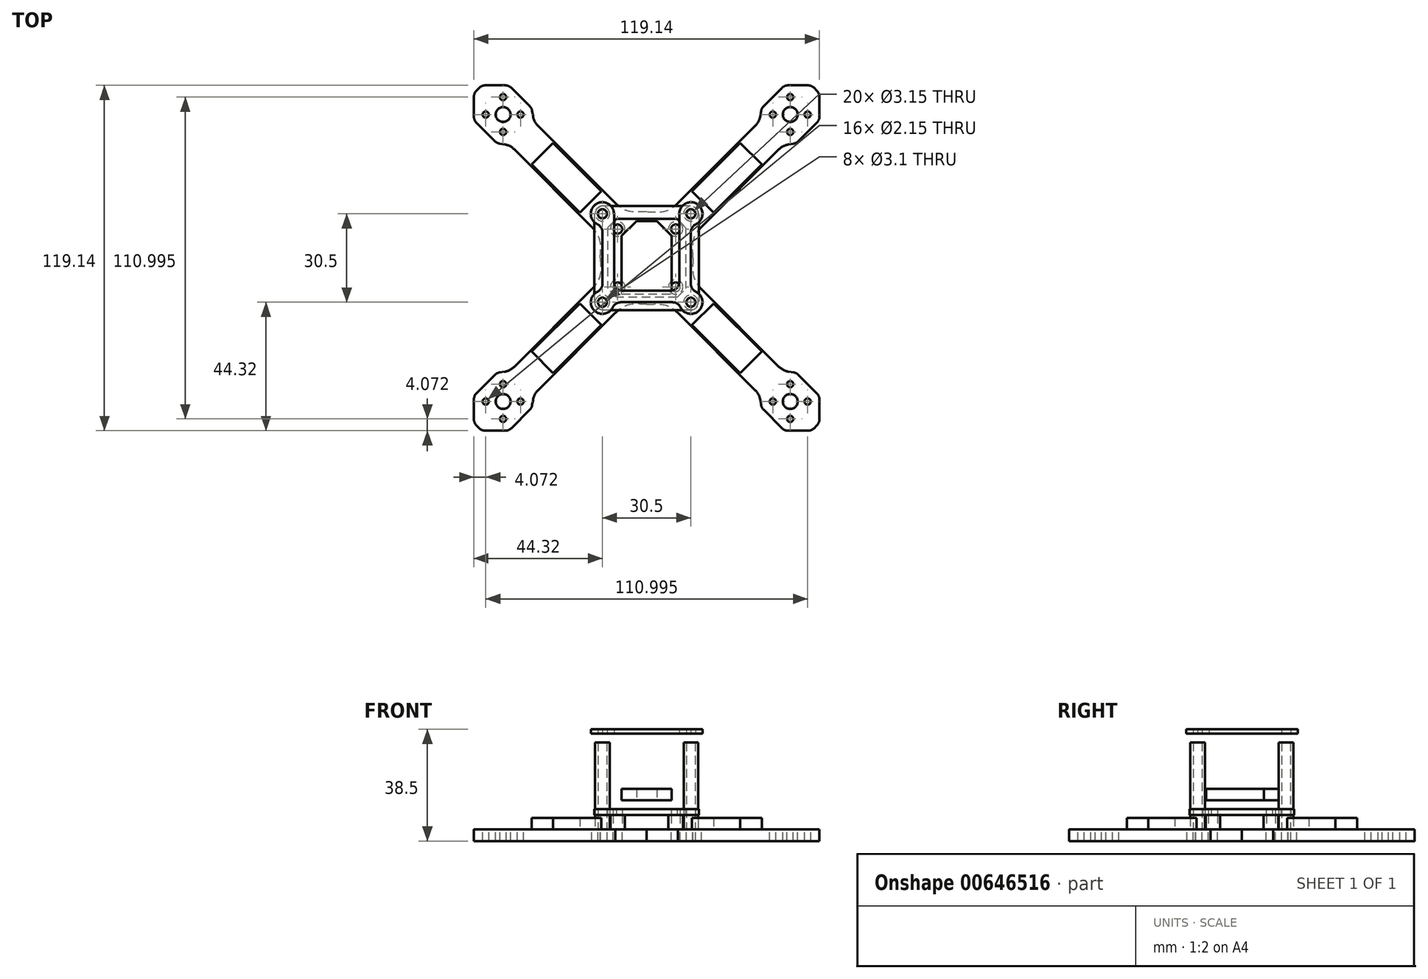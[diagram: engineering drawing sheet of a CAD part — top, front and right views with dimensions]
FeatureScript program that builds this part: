
annotation { "Feature Type Name" : "Feature", "Feature Type Description" : "" }
export const myFeature = defineFeature(function(context is Context, id is Id, definition is map)
    precondition{}
    {
        {
            var Q0;
            Q0=qCreatedBy(makeId("Top.planeOp"),FACE);
            var sketch = newSketch(context, id + "F0", { "sketchPlane" : qUnion([Q0])});
            skCircle(sketch, "E0.1", {"center": v(15.25, 15.25) * mm, "radius": 1.57 * mm});
            skLineSegment(sketch, "E1", {"start": v(49.5, 55.5) * mm, "end": v(49.5, 43.5) * mm, "construction": true});
            skLineSegment(sketch, "E2", {"start": v(45.25, 53.74) * mm, "end": v(53.74, 45.25) * mm, "construction": true});
            skCircle(sketch, "E3.MirrorC", {"center": v(49.5, 49.5) * mm, "radius": 2.58 * mm});
            skLineSegment(sketch, "E4", {"start": v(43.5, 49.5) * mm, "end": v(55.5, 49.5) * mm, "construction": true});
            skCircle(sketch, "E5", {"center": v(49.5, 49.5) * mm, "radius": 6 * mm, "construction": true});
            skCircle(sketch, "E6", {"center": v(43.5, 49.5) * mm, "radius": 1.07 * mm});
            skCircle(sketch, "E7.MirrorC", {"center": v(55.5, 49.5) * mm, "radius": 1.07 * mm});
            skCircle(sketch, "E8.MirrorC", {"center": v(49.5, 55.5) * mm, "radius": 1.07 * mm});
            skCircle(sketch, "E9.MirrorC", {"center": v(49.5, 43.5) * mm, "radius": 1.07 * mm});
            skLineSegment(sketch, "E10", {"start": v(0, 78.07) * mm, "end": v(0, -78.07) * mm, "construction": true});
            skLineSegment(sketch, "E11", {"start": v(-70, 0) * mm, "end": v(70, 0) * mm, "construction": true});
            skCircle(sketch, "E12.MirrorC", {"center": v(-15.25, 15.25) * mm, "radius": 1.57 * mm});
            skCircle(sketch, "E13.MirrorC", {"center": v(-15.25, -15.25) * mm, "radius": 1.57 * mm});
            skCircle(sketch, "E14.MirrorC", {"center": v(15.25, -15.25) * mm, "radius": 1.57 * mm});
            skLineSegment(sketch, "E15", {"start": v(49.5, 49.5) * mm, "end": v(-49.5, -49.5) * mm, "construction": true});
            skLineSegment(sketch, "E16", {"start": v(-49.5, 49.5) * mm, "end": v(49.5, -49.5) * mm, "construction": true});
            skLineSegment(sketch, "E17", {"start": v(10.78, 18.91) * mm, "end": v(18.91, 10.78) * mm, "construction": true});
            skPoint(sketch, "E18", {"position": v(14.85, 14.85) * mm});
            skPoint(sketch, "E19", {"position": v(0, 16) * mm});
            skLineSegment(sketch, "E20", {"start": v(49.5, 49.5) * mm, "end": v(67.48, 67.48) * mm, "construction": true});
            skCircle(sketch, "E21.MirrorC", {"center": v(55.5, -49.5) * mm, "radius": 1.07 * mm});
            skCircle(sketch, "E22.MirrorC", {"center": v(49.5, -43.5) * mm, "radius": 1.07 * mm});
            skLineSegment(sketch, "E23.MirrorCS", {"start": v(45.25, -53.74) * mm, "end": v(53.74, -45.25) * mm, "construction": true});
            skCircle(sketch, "E24.MirrorC", {"center": v(49.5, -55.5) * mm, "radius": 1.07 * mm});
            skLineSegment(sketch, "E25.MirrorCS", {"start": v(49.5, -55.5) * mm, "end": v(49.5, -43.5) * mm, "construction": true});
            skLineSegment(sketch, "E26.MirrorCS", {"start": v(43.5, -49.5) * mm, "end": v(55.5, -49.5) * mm, "construction": true});
            skCircle(sketch, "E27.MirrorC", {"center": v(43.5, -49.5) * mm, "radius": 1.07 * mm});
            skPoint(sketch, "E28.MirrorP", {"position": v(49.5, -49.5) * mm});
            skCircle(sketch, "E29.MirrorC", {"center": v(49.5, -49.5) * mm, "radius": 6 * mm, "construction": true});
            skCircle(sketch, "E30.MirrorC", {"center": v(49.5, -49.5) * mm, "radius": 2.58 * mm});
            skCircle(sketch, "E31.MirrorC", {"center": v(-49.5, -55.5) * mm, "radius": 1.07 * mm});
            skCircle(sketch, "E32.MirrorC", {"center": v(-43.5, -49.5) * mm, "radius": 1.07 * mm});
            skCircle(sketch, "E33.MirrorC", {"center": v(-55.5, -49.5) * mm, "radius": 1.07 * mm});
            skCircle(sketch, "E34.MirrorC", {"center": v(-49.5, -43.5) * mm, "radius": 1.07 * mm});
            skLineSegment(sketch, "E35.MirrorCS", {"start": v(-45.25, -53.74) * mm, "end": v(-53.74, -45.25) * mm, "construction": true});
            skLineSegment(sketch, "E36.MirrorCS", {"start": v(-43.5, -49.5) * mm, "end": v(-55.5, -49.5) * mm, "construction": true});
            skLineSegment(sketch, "E37.MirrorCS", {"start": v(-49.5, -55.5) * mm, "end": v(-49.5, -43.5) * mm, "construction": true});
            skPoint(sketch, "E38.MirrorP", {"position": v(-49.5, -49.5) * mm});
            skCircle(sketch, "E39.MirrorC", {"center": v(-49.5, -49.5) * mm, "radius": 6 * mm, "construction": true});
            skCircle(sketch, "E40.MirrorC", {"center": v(-49.5, -49.5) * mm, "radius": 2.58 * mm});
            skCircle(sketch, "E41.MirrorC", {"center": v(-49.5, 55.5) * mm, "radius": 1.07 * mm});
            skCircle(sketch, "E42.MirrorC", {"center": v(-43.5, 49.5) * mm, "radius": 1.07 * mm});
            skCircle(sketch, "E43.MirrorC", {"center": v(-49.5, 43.5) * mm, "radius": 1.07 * mm});
            skCircle(sketch, "E44.MirrorC", {"center": v(-55.5, 49.5) * mm, "radius": 1.07 * mm});
            skLineSegment(sketch, "E45.MirrorCS", {"start": v(-45.25, 53.74) * mm, "end": v(-53.74, 45.25) * mm, "construction": true});
            skLineSegment(sketch, "E46.MirrorCS", {"start": v(-43.5, 49.5) * mm, "end": v(-55.5, 49.5) * mm, "construction": true});
            skLineSegment(sketch, "E47.MirrorCS", {"start": v(-49.5, 55.5) * mm, "end": v(-49.5, 43.5) * mm, "construction": true});
            skPoint(sketch, "E48.MirrorP", {"position": v(-49.5, 49.5) * mm});
            skCircle(sketch, "E49.MirrorC", {"center": v(-49.5, 49.5) * mm, "radius": 6 * mm, "construction": true});
            skCircle(sketch, "E50.MirrorC", {"center": v(-49.5, 49.5) * mm, "radius": 2.58 * mm});
            skCircle(sketch, "E51.MirrorC", {"center": v(10, 10) * mm, "radius": 1.57 * mm});
            skCircle(sketch, "E52.MirrorC", {"center": v(10, -10) * mm, "radius": 1.57 * mm});
            skCircle(sketch, "E53.MirrorC", {"center": v(-10, -10) * mm, "radius": 1.57 * mm});
            skCircle(sketch, "E54.MirrorC", {"center": v(-10, 10) * mm, "radius": 1.57 * mm});
            skLineSegment(sketch, "E55", {"start": v(16, 8) * mm, "end": v(16, -8) * mm, "construction": true});
            skPoint(sketch, "E56", {"position": v(16, 0) * mm});
            skPoint(sketch, "E57", {"position": v(0, 0) * mm});
            skPoint(sketch, "E58", {"position": v(-27.66, 27.66) * mm});
            skPoint(sketch, "E59", {"position": v(6.88, 16.35) * mm});
            skFitSpline(sketch, "E60", {"points": [v(0, 16) * mm, v(6.88, 16.35) * mm, v(10.78, 18.91) * mm], "startDerivative": vector(12.86, -0.37) * mm, "endDerivative": vector(5.42, 4.33) * mm});
            skLineSegment(sketch, "E61", {"start": v(10.78, 18.91) * mm, "end": v(37.5, 45.63) * mm});
            skLineSegment(sketch, "E62", {"start": v(39.18, 48.92) * mm, "end": v(39.46, 50.68) * mm});
            skLineSegment(sketch, "E63", {"start": v(40.3, 52.33) * mm, "end": v(46.67, 58.69) * mm});
            skLineSegment(sketch, "E64", {"start": v(48.8, 59.57) * mm, "end": v(55.6, 59.57) * mm});
            skLineSegment(sketch, "E65", {"start": v(57.71, 58.69) * mm, "end": v(58.2, 58.2) * mm});
            skPoint(sketch, "E66.visualSharp", {"position": v(38.87, 47) * mm});
            skArc(sketch, "E66.filletArc", {"start": v(37.5, 45.63) * mm, "mid": v(38.6, 47.14) * mm, "end": v(39.18, 48.92) * mm});
            skPoint(sketch, "E67.visualSharp", {"position": v(39.62, 51.64) * mm});
            skArc(sketch, "E67.filletArc", {"start": v(40.3, 52.33) * mm, "mid": v(39.76, 51.57) * mm, "end": v(39.46, 50.68) * mm});
            skPoint(sketch, "E68.visualSharp", {"position": v(47.55, 59.57) * mm});
            skArc(sketch, "E68.filletArc", {"start": v(48.8, 59.57) * mm, "mid": v(47.64, 59.34) * mm, "end": v(46.67, 58.69) * mm});
            skPoint(sketch, "E69.visualSharp", {"position": v(56.84, 59.57) * mm});
            skArc(sketch, "E69.filletArc", {"start": v(57.71, 58.69) * mm, "mid": v(56.74, 59.34) * mm, "end": v(55.6, 59.57) * mm});
            skLineSegment(sketch, "E70.MirrorCS", {"start": v(52.33, 40.3) * mm, "end": v(58.69, 46.67) * mm});
            skPoint(sketch, "E71.MirrorP", {"position": v(47, 38.87) * mm});
            skArc(sketch, "E72.MirrorCS", {"start": v(52.33, 40.3) * mm, "mid": v(51.57, 39.76) * mm, "end": v(50.68, 39.46) * mm});
            skArc(sketch, "E73.MirrorCS", {"start": v(45.63, 37.5) * mm, "mid": v(47.14, 38.6) * mm, "end": v(48.92, 39.18) * mm});
            skPoint(sketch, "E74.MirrorP", {"position": v(51.64, 39.62) * mm});
            skArc(sketch, "E75.MirrorCS", {"start": v(59.57, 48.8) * mm, "mid": v(59.34, 47.64) * mm, "end": v(58.69, 46.67) * mm});
            skArc(sketch, "E76.MirrorCS", {"start": v(58.69, 57.71) * mm, "mid": v(59.34, 56.74) * mm, "end": v(59.57, 55.6) * mm});
            skPoint(sketch, "E77.MirrorP", {"position": v(59.57, 56.84) * mm});
            skLineSegment(sketch, "E78.MirrorCS", {"start": v(58.69, 57.71) * mm, "end": v(58.2, 58.2) * mm});
            skLineSegment(sketch, "E79.MirrorCS", {"start": v(59.57, 48.8) * mm, "end": v(59.57, 55.6) * mm});
            skPoint(sketch, "E80.MirrorP", {"position": v(59.57, 47.55) * mm});
            skLineSegment(sketch, "E81.MirrorCS", {"start": v(18.91, 10.78) * mm, "end": v(45.63, 37.5) * mm});
            skLineSegment(sketch, "E82.MirrorCS", {"start": v(48.92, 39.18) * mm, "end": v(50.68, 39.46) * mm});
            skFitSpline(sketch, "E83.MirrorCS", {"points": [v(16, 0) * mm, v(16.35, 6.88) * mm, v(18.91, 10.78) * mm], "startDerivative": vector(-0.37, 12.86) * mm, "endDerivative": vector(4.33, 5.42) * mm});
            skLineSegment(sketch, "E84", {"start": v(48.8, 56.57) * mm, "end": v(42.43, 50.2) * mm, "construction": true});
            skPoint(sketch, "E85", {"position": v(45.6, 53.39) * mm});
            skLineSegment(sketch, "E86.MirrorCS", {"start": v(57.71, -58.69) * mm, "end": v(58.2, -58.2) * mm});
            skLineSegment(sketch, "E87.MirrorCS", {"start": v(48.92, -39.18) * mm, "end": v(50.68, -39.46) * mm});
            skLineSegment(sketch, "E88.MirrorCS", {"start": v(39.18, -48.92) * mm, "end": v(39.46, -50.68) * mm});
            skLineSegment(sketch, "E89.MirrorCS", {"start": v(58.69, -57.71) * mm, "end": v(58.2, -58.2) * mm});
            skArc(sketch, "E90.MirrorCS", {"start": v(48.8, -59.57) * mm, "mid": v(47.64, -59.34) * mm, "end": v(46.67, -58.69) * mm});
            skArc(sketch, "E91.MirrorCS", {"start": v(37.5, -45.63) * mm, "mid": v(38.6, -47.14) * mm, "end": v(39.18, -48.92) * mm});
            skArc(sketch, "E92.MirrorCS", {"start": v(57.71, -58.69) * mm, "mid": v(56.74, -59.34) * mm, "end": v(55.6, -59.57) * mm});
            skArc(sketch, "E93.MirrorCS", {"start": v(45.63, -37.5) * mm, "mid": v(47.14, -38.6) * mm, "end": v(48.92, -39.18) * mm});
            skArc(sketch, "E94.MirrorCS", {"start": v(59.57, -48.8) * mm, "mid": v(59.34, -47.64) * mm, "end": v(58.69, -46.67) * mm});
            skArc(sketch, "E95.MirrorCS", {"start": v(52.33, -40.3) * mm, "mid": v(51.57, -39.76) * mm, "end": v(50.68, -39.46) * mm});
            skArc(sketch, "E96.MirrorCS", {"start": v(58.69, -57.71) * mm, "mid": v(59.34, -56.74) * mm, "end": v(59.57, -55.6) * mm});
            skArc(sketch, "E97.MirrorCS", {"start": v(40.3, -52.33) * mm, "mid": v(39.76, -51.57) * mm, "end": v(39.46, -50.68) * mm});
            skLineSegment(sketch, "E98.MirrorCS", {"start": v(48.8, -56.57) * mm, "end": v(42.43, -50.2) * mm, "construction": true});
            skFitSpline(sketch, "E99.MirrorCS", {"points": [v(16, 0) * mm, v(16.35, -6.88) * mm, v(18.91, -10.78) * mm], "startDerivative": vector(-0.37, -12.86) * mm, "endDerivative": vector(4.33, -5.42) * mm});
            skFitSpline(sketch, "E100.MirrorCS", {"points": [v(0, -16) * mm, v(6.88, -16.35) * mm, v(10.78, -18.91) * mm], "startDerivative": vector(12.86, 0.37) * mm, "endDerivative": vector(5.42, -4.33) * mm});
            skPoint(sketch, "E101.MirrorP", {"position": v(59.57, -47.55) * mm});
            skLineSegment(sketch, "E102.MirrorCS", {"start": v(52.33, -40.3) * mm, "end": v(58.69, -46.67) * mm});
            skLineSegment(sketch, "E103.MirrorCS", {"start": v(40.3, -52.33) * mm, "end": v(46.67, -58.69) * mm});
            skPoint(sketch, "E104.MirrorP", {"position": v(47.55, -59.57) * mm});
            skPoint(sketch, "E105.MirrorP", {"position": v(38.87, -47) * mm});
            skPoint(sketch, "E106.MirrorP", {"position": v(47, -38.87) * mm});
            skLineSegment(sketch, "E107.MirrorCS", {"start": v(10.78, -18.91) * mm, "end": v(37.5, -45.63) * mm});
            skPoint(sketch, "E108.MirrorP", {"position": v(39.62, -51.64) * mm});
            skLineSegment(sketch, "E109.MirrorCS", {"start": v(59.57, -48.8) * mm, "end": v(59.57, -55.6) * mm});
            skPoint(sketch, "E110.MirrorP", {"position": v(51.64, -39.62) * mm});
            skPoint(sketch, "E111.MirrorP", {"position": v(59.57, -56.84) * mm});
            skPoint(sketch, "E112.MirrorP", {"position": v(45.6, -53.39) * mm});
            skLineSegment(sketch, "E113.MirrorCS", {"start": v(48.8, -59.57) * mm, "end": v(55.6, -59.57) * mm});
            skPoint(sketch, "E114.MirrorP", {"position": v(56.84, -59.57) * mm});
            skLineSegment(sketch, "E115.MirrorCS", {"start": v(18.91, -10.78) * mm, "end": v(45.63, -37.5) * mm});
            skLineSegment(sketch, "E116.MirrorCS", {"start": v(-57.71, 58.69) * mm, "end": v(-58.2, 58.2) * mm});
            skLineSegment(sketch, "E117.MirrorCS", {"start": v(-58.69, -57.71) * mm, "end": v(-58.2, -58.2) * mm});
            skLineSegment(sketch, "E118.MirrorCS", {"start": v(-39.18, -48.92) * mm, "end": v(-39.46, -50.68) * mm});
            skArc(sketch, "E119.MirrorCS", {"start": v(-40.3, -52.33) * mm, "mid": v(-39.76, -51.57) * mm, "end": v(-39.46, -50.68) * mm});
            skArc(sketch, "E120.MirrorCS", {"start": v(-37.5, -45.63) * mm, "mid": v(-38.6, -47.14) * mm, "end": v(-39.18, -48.92) * mm});
            skArc(sketch, "E121.MirrorCS", {"start": v(-45.63, -37.5) * mm, "mid": v(-47.14, -38.6) * mm, "end": v(-48.92, -39.18) * mm});
            skLineSegment(sketch, "E122.MirrorCS", {"start": v(-39.18, 48.92) * mm, "end": v(-39.46, 50.68) * mm});
            skArc(sketch, "E123.MirrorCS", {"start": v(-59.57, -48.8) * mm, "mid": v(-59.34, -47.64) * mm, "end": v(-58.69, -46.67) * mm});
            skArc(sketch, "E124.MirrorCS", {"start": v(-58.69, 57.71) * mm, "mid": v(-59.34, 56.74) * mm, "end": v(-59.57, 55.6) * mm});
            skArc(sketch, "E125.MirrorCS", {"start": v(-57.71, -58.69) * mm, "mid": v(-56.74, -59.34) * mm, "end": v(-55.6, -59.57) * mm});
            skArc(sketch, "E126.MirrorCS", {"start": v(-57.71, 58.69) * mm, "mid": v(-56.74, 59.34) * mm, "end": v(-55.6, 59.57) * mm});
            skLineSegment(sketch, "E127.MirrorCS", {"start": v(-57.71, -58.69) * mm, "end": v(-58.2, -58.2) * mm});
            skLineSegment(sketch, "E128.MirrorCS", {"start": v(-48.92, 39.18) * mm, "end": v(-50.68, 39.46) * mm});
            skLineSegment(sketch, "E129.MirrorCS", {"start": v(-48.92, -39.18) * mm, "end": v(-50.68, -39.46) * mm});
            skLineSegment(sketch, "E130.MirrorCS", {"start": v(-58.69, 57.71) * mm, "end": v(-58.2, 58.2) * mm});
            skArc(sketch, "E131.MirrorCS", {"start": v(-59.57, 48.8) * mm, "mid": v(-59.34, 47.64) * mm, "end": v(-58.69, 46.67) * mm});
            skArc(sketch, "E132.MirrorCS", {"start": v(-40.3, 52.33) * mm, "mid": v(-39.76, 51.57) * mm, "end": v(-39.46, 50.68) * mm});
            skArc(sketch, "E133.MirrorCS", {"start": v(-45.63, 37.5) * mm, "mid": v(-47.14, 38.6) * mm, "end": v(-48.92, 39.18) * mm});
            skArc(sketch, "E134.MirrorCS", {"start": v(-58.69, -57.71) * mm, "mid": v(-59.34, -56.74) * mm, "end": v(-59.57, -55.6) * mm});
            skArc(sketch, "E135.MirrorCS", {"start": v(-52.33, -40.3) * mm, "mid": v(-51.57, -39.76) * mm, "end": v(-50.68, -39.46) * mm});
            skArc(sketch, "E136.MirrorCS", {"start": v(-48.8, 59.57) * mm, "mid": v(-47.64, 59.34) * mm, "end": v(-46.67, 58.69) * mm});
            skArc(sketch, "E137.MirrorCS", {"start": v(-48.8, -59.57) * mm, "mid": v(-47.64, -59.34) * mm, "end": v(-46.67, -58.69) * mm});
            skArc(sketch, "E138.MirrorCS", {"start": v(-37.5, 45.63) * mm, "mid": v(-38.6, 47.14) * mm, "end": v(-39.18, 48.92) * mm});
            skArc(sketch, "E139.MirrorCS", {"start": v(-52.33, 40.3) * mm, "mid": v(-51.57, 39.76) * mm, "end": v(-50.68, 39.46) * mm});
            skFitSpline(sketch, "E140.MirrorCS", {"points": [v(-16, 0) * mm, v(-16.35, 6.88) * mm, v(-18.91, 10.78) * mm], "startDerivative": vector(0.37, 12.86) * mm, "endDerivative": vector(-4.33, 5.42) * mm});
            skFitSpline(sketch, "E141.MirrorCS", {"points": [v(0, -16) * mm, v(-6.88, -16.35) * mm, v(-10.78, -18.91) * mm], "startDerivative": vector(-12.86, 0.37) * mm, "endDerivative": vector(-5.42, -4.33) * mm});
            skLineSegment(sketch, "E142.MirrorCS", {"start": v(-48.8, -56.57) * mm, "end": v(-42.43, -50.2) * mm, "construction": true});
            skFitSpline(sketch, "E143.MirrorCS", {"points": [v(0, 16) * mm, v(-6.88, 16.35) * mm, v(-10.78, 18.91) * mm], "startDerivative": vector(-12.86, -0.37) * mm, "endDerivative": vector(-5.42, 4.33) * mm});
            skFitSpline(sketch, "E144.MirrorCS", {"points": [v(-16, 0) * mm, v(-16.35, -6.88) * mm, v(-18.91, -10.78) * mm], "startDerivative": vector(0.37, -12.86) * mm, "endDerivative": vector(-4.33, -5.42) * mm});
            skLineSegment(sketch, "E145.MirrorCS", {"start": v(-48.8, 56.57) * mm, "end": v(-42.43, 50.2) * mm, "construction": true});
            skLineSegment(sketch, "E146.MirrorCS", {"start": v(-40.3, -52.33) * mm, "end": v(-46.67, -58.69) * mm});
            skLineSegment(sketch, "E147.MirrorCS", {"start": v(-48.8, -59.57) * mm, "end": v(-55.6, -59.57) * mm});
            skPoint(sketch, "E148.MirrorP", {"position": v(-39.62, 51.64) * mm});
            skPoint(sketch, "E149.MirrorP", {"position": v(-47.55, -59.57) * mm});
            skPoint(sketch, "E150.MirrorP", {"position": v(-45.6, -53.39) * mm});
            skLineSegment(sketch, "E151.MirrorCS", {"start": v(-49.5, 49.5) * mm, "end": v(-67.48, 67.48) * mm, "construction": true});
            skPoint(sketch, "E152.MirrorP", {"position": v(-38.87, 47) * mm});
            skLineSegment(sketch, "E153.MirrorCS", {"start": v(-10.78, 18.91) * mm, "end": v(-37.5, 45.63) * mm});
            skLineSegment(sketch, "E154.MirrorCS", {"start": v(-40.3, 52.33) * mm, "end": v(-46.67, 58.69) * mm});
            skPoint(sketch, "E155.MirrorP", {"position": v(-51.64, -39.62) * mm});
            skPoint(sketch, "E156.MirrorP", {"position": v(-59.57, 47.55) * mm});
            skLineSegment(sketch, "E157.MirrorCS", {"start": v(-52.33, -40.3) * mm, "end": v(-58.69, -46.67) * mm});
            skPoint(sketch, "E158.MirrorP", {"position": v(-56.84, 59.57) * mm});
            skPoint(sketch, "E159.MirrorP", {"position": v(-59.57, -47.55) * mm});
            skPoint(sketch, "E160.MirrorP", {"position": v(-59.57, 56.84) * mm});
            skLineSegment(sketch, "E161.MirrorCS", {"start": v(-18.91, 10.78) * mm, "end": v(-45.63, 37.5) * mm});
            skPoint(sketch, "E162.MirrorP", {"position": v(-38.87, -47) * mm});
            skLineSegment(sketch, "E163.MirrorCS", {"start": v(-59.57, 48.8) * mm, "end": v(-59.57, 55.6) * mm});
            skPoint(sketch, "E164.MirrorP", {"position": v(-47, -38.87) * mm});
            skPoint(sketch, "E165.MirrorP", {"position": v(-59.57, -56.84) * mm});
            skLineSegment(sketch, "E166.MirrorCS", {"start": v(-18.91, -10.78) * mm, "end": v(-45.63, -37.5) * mm});
            skPoint(sketch, "E167.MirrorP", {"position": v(-47, 38.87) * mm});
            skPoint(sketch, "E168.MirrorP", {"position": v(-47.55, 59.57) * mm});
            skLineSegment(sketch, "E169.MirrorCS", {"start": v(-52.33, 40.3) * mm, "end": v(-58.69, 46.67) * mm});
            skPoint(sketch, "E170.MirrorP", {"position": v(-56.84, -59.57) * mm});
            skLineSegment(sketch, "E171.MirrorCS", {"start": v(-10.78, -18.91) * mm, "end": v(-37.5, -45.63) * mm});
            skPoint(sketch, "E172.MirrorP", {"position": v(-51.64, 39.62) * mm});
            skLineSegment(sketch, "E173.MirrorCS", {"start": v(-59.57, -48.8) * mm, "end": v(-59.57, -55.6) * mm});
            skLineSegment(sketch, "E174.MirrorCS", {"start": v(-48.8, 59.57) * mm, "end": v(-55.6, 59.57) * mm});
            skPoint(sketch, "E175.MirrorP", {"position": v(-39.62, -51.64) * mm});
            skPoint(sketch, "E176.MirrorP", {"position": v(-45.6, 53.39) * mm});
            skLineSegment(sketch, "E177", {"start": v(45.25, 53.74) * mm, "end": v(40.94, 58.06) * mm, "construction": true});
            skPoint(sketch, "E178", {"position": v(43.49, 55.5) * mm});
            skSolve(sketch);
        }
        {
            var Q0;
            Q0=qCreatedBy(makeId("Top.planeOp"),FACE);
            cPlane(context, id + "F1", {"entities" : qUnion([Q0]), "cplaneType" : CPlaneType.OFFSET, "offset" : 20 * mm, "width" : 150 * mm, "height" : 150 * mm});
        }
        {
            var Q0;
            Q0=qSketchRegion(id+"F0",true);
            extrude(context, id + "F2", {"entities" : qUnion([Q0]), "oppositeDirection" : true, "depth" : 4 * mm, "offsetDistance" : 25 * mm});
        }
        {
            var Q0;
            Q0=qCreatedBy(makeId("Top.planeOp"),FACE);
            cPlane(context, id + "F3", {"entities" : qUnion([Q0]), "cplaneType" : CPlaneType.OFFSET, "offset" : 10 * mm, "width" : 150 * mm, "height" : 150 * mm});
        }
        {
            var Q0;
            Q0=qCreatedBy(id+"F3.planeOp",FACE);
            var sketch = newSketch(context, id + "F4", { "sketchPlane" : qUnion([Q0])});
            skLineSegment(sketch, "E179", {"start": v(-8.62, -12.37) * mm, "end": v(8.63, -12.37) * mm});
            skLineSegment(sketch, "E180", {"start": v(-8.62, -12.37) * mm, "end": v(-8.62, 7.63) * mm});
            skLineSegment(sketch, "E181", {"start": v(0, -12.37) * mm, "end": v(0, 12.78) * mm, "construction": true});
            skPoint(sketch, "E181.startSnap0", {"position": v(0, -12.37) * mm});
            skLineSegment(sketch, "E182", {"start": v(-3.5, 12.78) * mm, "end": v(3.5, 12.78) * mm});
            skPoint(sketch, "E183", {"position": v(0, 12.78) * mm});
            skLineSegment(sketch, "E184", {"start": v(-8.62, 7.63) * mm, "end": v(-3.5, 12.78) * mm});
            skLineSegment(sketch, "E185.MirrorCS", {"start": v(8.63, 7.63) * mm, "end": v(3.5, 12.78) * mm});
            skLineSegment(sketch, "E186.MirrorCS", {"start": v(8.63, -12.37) * mm, "end": v(8.63, 7.63) * mm});
            skSolve(sketch);
        }
        {
            var Q0;
            Q0=qSketchRegion(id+"F4",true);
            extrude(context, id + "F5", {"entities" : qUnion([Q0]), "depth" : 4 * mm});
        }
        {
            var Q0;
            Q0=qCreatedBy(makeId("Top.planeOp"),FACE);
            cPlane(context, id + "F6", {"entities" : qUnion([Q0]), "cplaneType" : CPlaneType.OFFSET, "offset" : 5 * mm, "width" : 150 * mm, "height" : 150 * mm});
        }
        {
            var Q0;
            Q0=qCreatedBy(id+"F6.planeOp",FACE);
            var sketch = newSketch(context, id + "F7", { "sketchPlane" : qUnion([Q0])});
            skLineSegment(sketch, "E187", {"start": v(0, 13.5) * mm, "end": v(0, -13.5) * mm, "construction": true});
            skLineSegment(sketch, "E188", {"start": v(-13.5, 0) * mm, "end": v(13.5, 0) * mm, "construction": true});
            skLineSegment(sketch, "E189", {"start": v(-13.5, 10.5) * mm, "end": v(-13.5, -10.5) * mm});
            skLineSegment(sketch, "E190", {"start": v(10.5, 13.5) * mm, "end": v(-10.5, 13.5) * mm});
            skLineSegment(sketch, "E191.MirrorCS", {"start": v(10.5, -13.5) * mm, "end": v(-10.5, -13.5) * mm});
            skLineSegment(sketch, "E192.MirrorCS", {"start": v(13.5, 10.5) * mm, "end": v(13.5, -10.5) * mm});
            skLineSegment(sketch, "E193", {"start": v(-10.5, 13.5) * mm, "end": v(-13.5, 10.5) * mm});
            skLineSegment(sketch, "E194.MirrorCS", {"start": v(-10.5, -13.5) * mm, "end": v(-13.5, -10.5) * mm});
            skLineSegment(sketch, "E195.MirrorCS", {"start": v(10.5, 13.5) * mm, "end": v(13.5, 10.5) * mm});
            skLineSegment(sketch, "E196.MirrorCS", {"start": v(10.5, -13.5) * mm, "end": v(13.5, -10.5) * mm});
            skCircle(sketch, "E197", {"center": v(-10, 10) * mm, "radius": 1.57 * mm});
            skLineSegment(sketch, "E198", {"start": v(-10, 10) * mm, "end": v(10, 10) * mm, "construction": true});
            skLineSegment(sketch, "E199", {"start": v(10, 10) * mm, "end": v(10, -10) * mm, "construction": true});
            skLineSegment(sketch, "E200", {"start": v(10, -10) * mm, "end": v(-10, -10) * mm, "construction": true});
            skLineSegment(sketch, "E201", {"start": v(-10, -10) * mm, "end": v(-10, 10) * mm, "construction": true});
            skPoint(sketch, "E202", {"position": v(0, 10) * mm});
            skPoint(sketch, "E203", {"position": v(-10, 0) * mm});
            skCircle(sketch, "E204.MirrorC", {"center": v(10, 10) * mm, "radius": 1.57 * mm});
            skCircle(sketch, "E205.MirrorC", {"center": v(-10, -10) * mm, "radius": 1.57 * mm});
            skCircle(sketch, "E206.MirrorC", {"center": v(10, -10) * mm, "radius": 1.57 * mm});
            skSolve(sketch);
        }
        {
            var Q0;
            Q0=qSketchRegion(id+"F7",true);
            extrude(context, id + "F8", {"entities" : qUnion([Q0]), "depth" : 2 * mm});
        }
        {
            var Q0;
            Q0=qCreatedBy(id+"F6.planeOp",FACE);
            var sketch = newSketch(context, id + "F9", { "sketchPlane" : qUnion([Q0])});
            skLineSegment(sketch, "E207", {"start": v(0, 18) * mm, "end": v(0, -18) * mm, "construction": true});
            skLineSegment(sketch, "E208", {"start": v(-18, 0) * mm, "end": v(18, 0) * mm, "construction": true});
            skCircle(sketch, "E209", {"center": v(-15.25, 15.25) * mm, "radius": 1.57 * mm});
            skLineSegment(sketch, "E210", {"start": v(-15.25, 15.25) * mm, "end": v(15.25, 15.25) * mm, "construction": true});
            skLineSegment(sketch, "E211", {"start": v(15.25, 15.25) * mm, "end": v(15.25, -15.25) * mm, "construction": true});
            skLineSegment(sketch, "E212", {"start": v(15.25, -15.25) * mm, "end": v(-15.25, -15.25) * mm, "construction": true});
            skLineSegment(sketch, "E213", {"start": v(-15.25, -15.25) * mm, "end": v(-15.25, 15.25) * mm, "construction": true});
            skPoint(sketch, "E214", {"position": v(0, 15.25) * mm});
            skPoint(sketch, "E215", {"position": v(-15.25, 0) * mm});
            skCircle(sketch, "E216.MirrorC", {"center": v(15.25, 15.25) * mm, "radius": 1.57 * mm});
            skCircle(sketch, "E217.MirrorC", {"center": v(-15.25, -15.25) * mm, "radius": 1.57 * mm});
            skCircle(sketch, "E218.MirrorC", {"center": v(15.25, -15.25) * mm, "radius": 1.57 * mm});
            skPoint(sketch, "E219", {"position": v(0, 0) * mm});
            skLineSegment(sketch, "E220.bottom", {"start": v(15, 18) * mm, "end": v(-15, 18) * mm});
            skLineSegment(sketch, "E220.top", {"start": v(15, -18) * mm, "end": v(-15, -18) * mm});
            skLineSegment(sketch, "E220.left", {"start": v(18, 15) * mm, "end": v(18, -15) * mm});
            skLineSegment(sketch, "E220.right", {"start": v(-18, 15) * mm, "end": v(-18, -15) * mm});
            skPoint(sketch, "E221.visualSharp", {"position": v(-18, 18) * mm});
            skArc(sketch, "E221.filletArc", {"start": v(-15, 18) * mm, "mid": v(-17.12, 17.12) * mm, "end": v(-18, 15) * mm});
            skPoint(sketch, "E222.visualSharp", {"position": v(18, 18) * mm});
            skArc(sketch, "E222.filletArc", {"start": v(18, 15) * mm, "mid": v(17.12, 17.12) * mm, "end": v(15, 18) * mm});
            skPoint(sketch, "E223.visualSharp", {"position": v(18, -18) * mm});
            skArc(sketch, "E223.filletArc", {"start": v(15, -18) * mm, "mid": v(17.12, -17.12) * mm, "end": v(18, -15) * mm});
            skPoint(sketch, "E224.visualSharp", {"position": v(-18, -18) * mm});
            skArc(sketch, "E224.filletArc", {"start": v(-18, -15) * mm, "mid": v(-17.12, -17.12) * mm, "end": v(-15, -18) * mm});
            skSolve(sketch);
        }
        {
            var Q0;
            Q0=qSketchRegion(id+"F9",true);
            extrude(context, id + "F10", {"entities" : qUnion([Q0]), "depth" : 2 * mm, "offsetDistance" : 25 * mm});
        }
        {
            var Q0;
            Q0=qCreatedBy(makeId("Top.planeOp"),FACE);
            var sketch = newSketch(context, id + "F11", { "sketchPlane" : qUnion([Q0])});
            skLineSegment(sketch, "E225.bottom", {"start": v(-39.68, 32.25) * mm, "end": v(-32.25, 39.68) * mm});
            skLineSegment(sketch, "E225.top", {"start": v(-23.06, 15.64) * mm, "end": v(-15.64, 23.06) * mm});
            skLineSegment(sketch, "E225.left", {"start": v(-39.68, 32.25) * mm, "end": v(-23.06, 15.64) * mm});
            skLineSegment(sketch, "E225.right", {"start": v(-32.25, 39.68) * mm, "end": v(-15.64, 23.06) * mm});
            skLineSegment(sketch, "E226", {"start": v(-23.95, 31.37) * mm, "end": v(-31.37, 23.95) * mm, "construction": true});
            skLineSegment(sketch, "E227.MirrorCS", {"start": v(23.95, 31.37) * mm, "end": v(31.37, 23.95) * mm, "construction": true});
            skLineSegment(sketch, "E228.MirrorCS", {"start": v(23.06, 15.64) * mm, "end": v(15.64, 23.06) * mm});
            skLineSegment(sketch, "E229.MirrorCS", {"start": v(39.68, 32.25) * mm, "end": v(32.25, 39.68) * mm});
            skLineSegment(sketch, "E230.MirrorCS", {"start": v(39.68, 32.25) * mm, "end": v(23.06, 15.64) * mm});
            skLineSegment(sketch, "E231.MirrorCS", {"start": v(32.25, 39.68) * mm, "end": v(15.64, 23.06) * mm});
            skLineSegment(sketch, "E232.MirrorCS", {"start": v(23.06, -15.64) * mm, "end": v(15.64, -23.06) * mm});
            skLineSegment(sketch, "E233.MirrorCS", {"start": v(32.25, -39.68) * mm, "end": v(15.64, -23.06) * mm});
            skLineSegment(sketch, "E234.MirrorCS", {"start": v(39.68, -32.25) * mm, "end": v(32.25, -39.68) * mm});
            skLineSegment(sketch, "E235.MirrorCS", {"start": v(39.68, -32.25) * mm, "end": v(23.06, -15.64) * mm});
            skLineSegment(sketch, "E236.MirrorCS", {"start": v(-39.68, -32.25) * mm, "end": v(-23.06, -15.64) * mm});
            skLineSegment(sketch, "E237.MirrorCS", {"start": v(-23.06, -15.64) * mm, "end": v(-15.64, -23.06) * mm});
            skLineSegment(sketch, "E238.MirrorCS", {"start": v(23.95, -31.37) * mm, "end": v(31.37, -23.95) * mm, "construction": true});
            skLineSegment(sketch, "E239.MirrorCS", {"start": v(-32.25, -39.68) * mm, "end": v(-15.64, -23.06) * mm});
            skLineSegment(sketch, "E240.MirrorCS", {"start": v(-23.95, -31.37) * mm, "end": v(-31.37, -23.95) * mm, "construction": true});
            skLineSegment(sketch, "E241.MirrorCS", {"start": v(-39.68, -32.25) * mm, "end": v(-32.25, -39.68) * mm});
            skSolve(sketch);
        }
        {
            var Q0;
            Q0=qSketchRegion(id+"F11",true);
            extrude(context, id + "F12", {"entities" : qUnion([Q0]), "operationType" : NewBodyOperationType.ADD, "depth" : 4 * mm, "offsetDistance" : 25 * mm});
        }
        {
            var Q0;
            Q0=qCreatedBy(makeId("Top.planeOp"),FACE);
            var sketch = newSketch(context, id + "F13", { "sketchPlane" : qUnion([Q0])});
            skCircle(sketch, "E242", {"center": v(15.25, 15.25) * mm, "radius": 2.5 * mm});
            skCircle(sketch, "E243.MirrorC", {"center": v(15.25, -15.25) * mm, "radius": 2.5 * mm});
            skCircle(sketch, "E244.MirrorC", {"center": v(-15.25, -15.25) * mm, "radius": 2.5 * mm});
            skCircle(sketch, "E245.MirrorC", {"center": v(-15.25, 15.25) * mm, "radius": 2.5 * mm});
            skCircle(sketch, "E246", {"center": v(15.25, 15.25) * mm, "radius": 1.55 * mm});
            skCircle(sketch, "E247.MirrorC", {"center": v(-15.25, 15.25) * mm, "radius": 1.55 * mm});
            skCircle(sketch, "E248.MirrorC", {"center": v(15.25, -15.25) * mm, "radius": 1.55 * mm});
            skCircle(sketch, "E249.MirrorC", {"center": v(-15.25, -15.25) * mm, "radius": 1.55 * mm});
            skSolve(sketch);
        }
        {
            var Q0;
            Q0=qSketchRegion(id+"F13",true);
            extrude(context, id + "F14", {"entities" : qUnion([Q0]), "depth" : 30 * mm, "offsetDistance" : 25 * mm});
        }
        {
            var Q0;
            Q0=qCreatedBy(makeId("Top.planeOp"),FACE);
            var sketch = newSketch(context, id + "F15", { "sketchPlane" : qUnion([Q0])});
            skCircle(sketch, "E250", {"center": v(10, 10) * mm, "radius": 2.5 * mm});
            skCircle(sketch, "E251.MirrorC", {"center": v(10, -10) * mm, "radius": 2.5 * mm});
            skCircle(sketch, "E252.MirrorC", {"center": v(-10, -10) * mm, "radius": 2.5 * mm});
            skCircle(sketch, "E253.MirrorC", {"center": v(-10, 10) * mm, "radius": 2.5 * mm});
            skCircle(sketch, "E254", {"center": v(10, 10) * mm, "radius": 1.55 * mm});
            skCircle(sketch, "E255.MirrorC", {"center": v(10, -10) * mm, "radius": 1.55 * mm});
            skCircle(sketch, "E256.MirrorC", {"center": v(-10, 10) * mm, "radius": 1.55 * mm});
            skCircle(sketch, "E257.MirrorC", {"center": v(-10, -10) * mm, "radius": 1.55 * mm});
            skSolve(sketch);
        }
        {
            var Q0;
            Q0=qSketchRegion(id+"F15",true);
            extrude(context, id + "F16", {"entities" : qUnion([Q0]), "depth" : 5 * mm, "offsetDistance" : 25 * mm});
        }
        {
            var Q0;
            Q0=qCreatedBy(makeId("Top.planeOp"),FACE);
            cPlane(context, id + "F17", {"entities" : qUnion([Q0]), "cplaneType" : CPlaneType.OFFSET, "offset" : 33 * mm, "width" : 150 * mm, "height" : 150 * mm});
        }
        {
            var Q0;
            Q0=qCreatedBy(id+"F17.planeOp",FACE);
            var sketch = newSketch(context, id + "F18", { "sketchPlane" : qUnion([Q0])});
            skLineSegment(sketch, "E258", {"start": v(15.25, 15.25) * mm, "end": v(-15.25, 15.25) * mm, "construction": true});
            skLineSegment(sketch, "E259", {"start": v(-15.25, 15.25) * mm, "end": v(-15.25, -15.25) * mm, "construction": true});
            skLineSegment(sketch, "E260", {"start": v(-15.25, -15.25) * mm, "end": v(15.25, -15.25) * mm, "construction": true});
            skLineSegment(sketch, "E261", {"start": v(15.25, -15.25) * mm, "end": v(15.25, 15.25) * mm, "construction": true});
            skArc(sketch, "E262", {"start": v(-11.25, 15.25) * mm, "mid": v(-17.39, 18.63) * mm, "end": v(-16.96, 11.64) * mm});
            skCircle(sketch, "E263", {"center": v(-15.25, 15.25) * mm, "radius": 1.57 * mm});
            skCircle(sketch, "E264.MirrorC", {"center": v(15.25, 15.25) * mm, "radius": 1.57 * mm});
            skArc(sketch, "E265.MirrorCS", {"start": v(11.25, 15.25) * mm, "mid": v(17.39, 18.63) * mm, "end": v(16.96, 11.64) * mm});
            skLineSegment(sketch, "E266.MirrorCS", {"start": v(8.93, -15.25) * mm, "end": v(-8.93, -15.25) * mm});
            skArc(sketch, "E267.MirrorCS", {"start": v(11.64, -16.96) * mm, "mid": v(18.08, -18.08) * mm, "end": v(16.96, -11.64) * mm});
            skCircle(sketch, "E268.MirrorC", {"center": v(15.25, -15.25) * mm, "radius": 1.57 * mm});
            skCircle(sketch, "E269.MirrorC", {"center": v(-15.25, -15.25) * mm, "radius": 1.57 * mm});
            skArc(sketch, "E270.MirrorCS", {"start": v(-11.64, -16.96) * mm, "mid": v(-18.08, -18.08) * mm, "end": v(-16.96, -11.64) * mm});
            skLineSegment(sketch, "E271", {"start": v(-15.25, 8.93) * mm, "end": v(-15.25, -8.93) * mm});
            skLineSegment(sketch, "E272.MirrorCS", {"start": v(15.25, 8.93) * mm, "end": v(15.25, -8.93) * mm});
            skLineSegment(sketch, "E273", {"start": v(11.25, 15.25) * mm, "end": v(11.25, -8.25) * mm});
            skLineSegment(sketch, "E274.MirrorCS", {"start": v(-11.25, 15.25) * mm, "end": v(-11.25, -8.25) * mm});
            skLineSegment(sketch, "E275", {"start": v(-8.25, -11.25) * mm, "end": v(8.25, -11.25) * mm});
            skPoint(sketch, "E276.visualSharp", {"position": v(-15.25, 11.25) * mm});
            skArc(sketch, "E276.filletArc", {"start": v(-15.25, 8.93) * mm, "mid": v(-15.71, 10.53) * mm, "end": v(-16.96, 11.64) * mm});
            skPoint(sketch, "E277.visualSharp", {"position": v(-15.25, -11.25) * mm});
            skArc(sketch, "E277.filletArc", {"start": v(-16.96, -11.64) * mm, "mid": v(-15.71, -10.53) * mm, "end": v(-15.25, -8.93) * mm});
            skPoint(sketch, "E278.visualSharp", {"position": v(-11.25, -15.25) * mm});
            skArc(sketch, "E278.filletArc", {"start": v(-8.93, -15.25) * mm, "mid": v(-10.53, -15.71) * mm, "end": v(-11.64, -16.96) * mm});
            skPoint(sketch, "E279.visualSharp", {"position": v(-11.25, -11.25) * mm});
            skArc(sketch, "E279.filletArc", {"start": v(-11.25, -8.25) * mm, "mid": v(-10.37, -10.37) * mm, "end": v(-8.25, -11.25) * mm});
            skPoint(sketch, "E280.visualSharp", {"position": v(11.25, -11.25) * mm});
            skArc(sketch, "E280.filletArc", {"start": v(8.25, -11.25) * mm, "mid": v(10.37, -10.37) * mm, "end": v(11.25, -8.25) * mm});
            skPoint(sketch, "E281.visualSharp", {"position": v(11.25, -15.25) * mm});
            skArc(sketch, "E281.filletArc", {"start": v(11.64, -16.96) * mm, "mid": v(10.53, -15.71) * mm, "end": v(8.93, -15.25) * mm});
            skPoint(sketch, "E282.visualSharp", {"position": v(15.25, -11.25) * mm});
            skArc(sketch, "E282.filletArc", {"start": v(15.25, -8.93) * mm, "mid": v(15.71, -10.53) * mm, "end": v(16.96, -11.64) * mm});
            skPoint(sketch, "E283.visualSharp", {"position": v(15.25, 11.25) * mm});
            skArc(sketch, "E283.filletArc", {"start": v(16.96, 11.64) * mm, "mid": v(15.71, 10.53) * mm, "end": v(15.25, 8.93) * mm});
            skLineSegment(sketch, "E284", {"start": v(-15.25, -4.8) * mm, "end": v(-11.25, -4.8) * mm, "construction": true});
            skLineSegment(sketch, "E285", {"start": v(-4.76, -11.25) * mm, "end": v(-4.76, -15.25) * mm, "construction": true});
            skSolve(sketch);
        }
        {
            var Q0;
            Q0=qSketchRegion(id+"F18",true);
            extrude(context, id + "F19", {"entities" : qUnion([Q0]), "depth" : 1.5 * mm, "offsetDistance" : 25 * mm});
        }
    });
